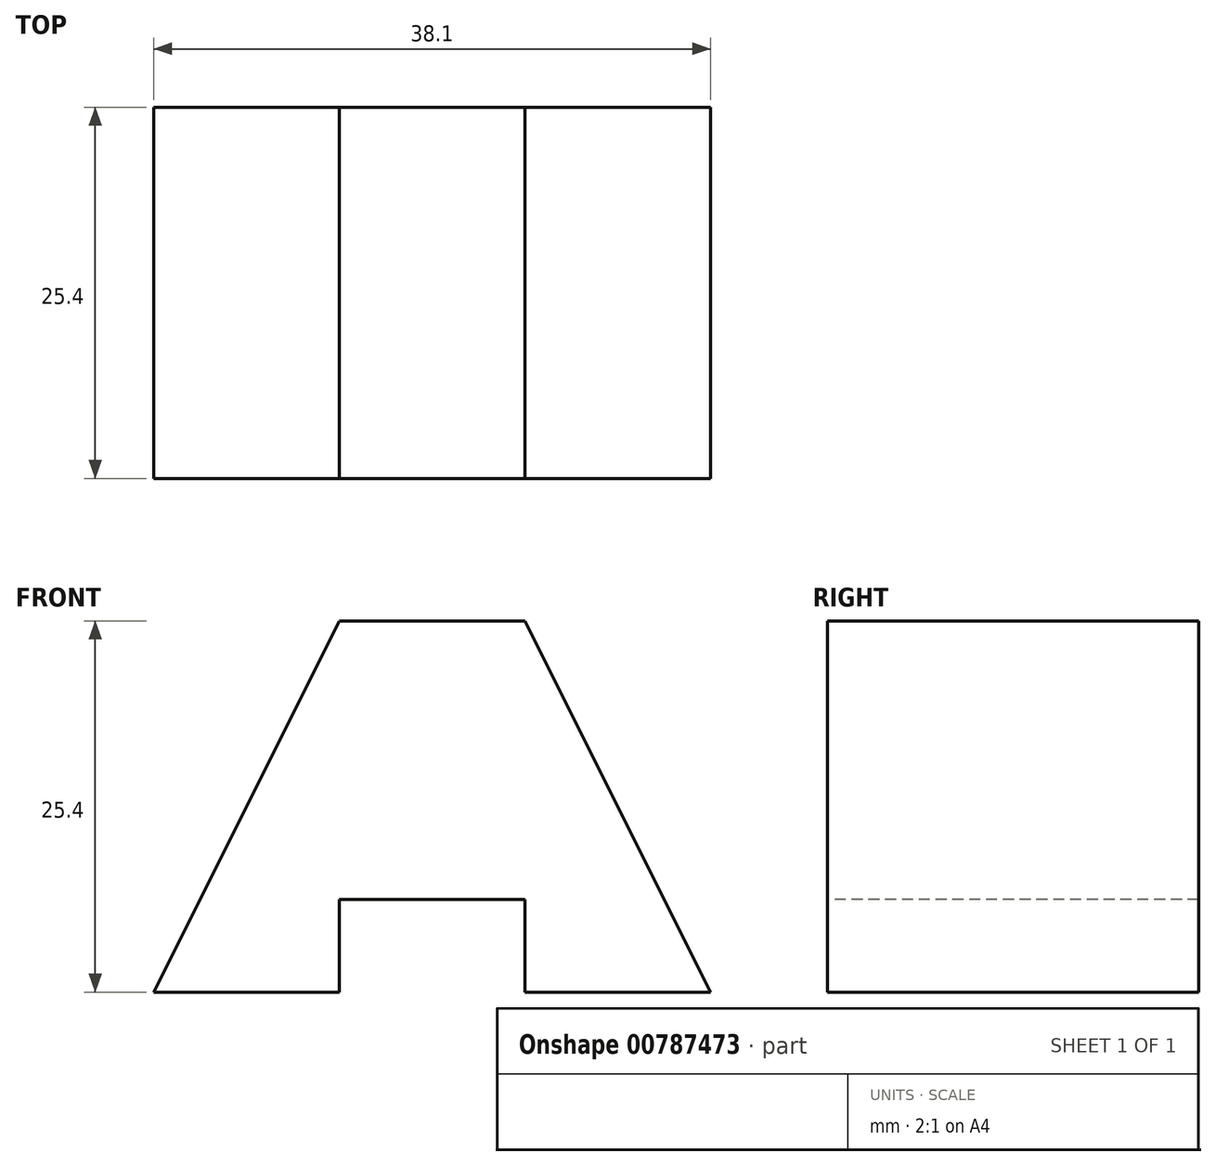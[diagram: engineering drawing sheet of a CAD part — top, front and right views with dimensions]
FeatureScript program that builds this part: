
annotation { "Feature Type Name" : "Feature", "Feature Type Description" : "" }
export const myFeature = defineFeature(function(context is Context, id is Id, definition is map)
    precondition{}
    {
        {
            var Q0;
            Q0=qCreatedBy(makeId("Front.planeOp"),FACE);
            var sketch = newSketch(context, id + "F0", { "sketchPlane" : qUnion([Q0])});
            skLineSegment(sketch, "E0", {"start": v(3, 0) * mm, "end": v(41.1, 0) * mm});
            skLineSegment(sketch, "E1", {"start": v(41.1, 0) * mm, "end": v(41.1, 25.4) * mm});
            skLineSegment(sketch, "E2", {"start": v(41.1, 25.4) * mm, "end": v(3, 25.4) * mm});
            skLineSegment(sketch, "E3", {"start": v(3, 0) * mm, "end": v(3, 25.4) * mm});
            skSolve(sketch);
        }
        {
            var Q0;
            Q0 = qSketchRegion(id + "F0", true);
            extrude(context, id + "F1", {"entities" : qUnion([Q0]), "depth" : 25.4 * mm, "offsetDistance" : 25.4 * mm});
        }
        {
            var Q0;
            Q0=makeQuery(id+"F1.opExtrude","CAP_FACE",FACE,{"disambiguationData":[OSD([sQuery(id+"F0.wireOp",EDGE,"E0"),sQuery(id+"F0.wireOp",EDGE,"E1"),sQuery(id+"F0.wireOp",EDGE,"E2"),sQuery(id+"F0.wireOp",EDGE,"E3")])],"isStart":false});
            var sketch = newSketch(context, id + "F2", { "sketchPlane" : qUnion([Q0])});
            skLineSegment(sketch, "E4", {"start": v(3, 0) * mm, "end": v(15.7, 0) * mm});
            skLineSegment(sketch, "E5", {"start": v(15.7, 0) * mm, "end": v(15.7, 6.35) * mm});
            skLineSegment(sketch, "E6", {"start": v(15.7, 6.35) * mm, "end": v(28.4, 6.35) * mm});
            skLineSegment(sketch, "E7", {"start": v(28.4, 6.35) * mm, "end": v(28.4, 0) * mm});
            skSolve(sketch);
        }
        {
            var Q0;
            Q0 = qSketchRegion(id + "F2", true);
            var Q1;
            {var subQ0=sQuery(id+"F2.wireOp",EDGE,"E5");Q1=makeQuery(id+"F2.imprint","IMPRINT",FACE,{"disambiguationData":[TD([[makeQuery(id+"F2.imprint","IMPRINT",EDGE,{"derivedFrom":subQ0}),-1.0]])]});}
            extrude(context, id + "F3", {"entities" : qUnion([Q0, Q1]), "operationType" : NewBodyOperationType.REMOVE, "oppositeDirection" : true, "depth" : 25.4 * mm, "offsetDistance" : 25.4 * mm});
        }
        {
            var Q0;
            Q0=makeQuery(id+"F1.opExtrude","CAP_FACE",FACE,{"disambiguationData":[OSD([sQuery(id+"F0.wireOp",EDGE,"E0"),sQuery(id+"F0.wireOp",EDGE,"E1"),sQuery(id+"F0.wireOp",EDGE,"E2"),sQuery(id+"F0.wireOp",EDGE,"E3")])],"isStart":false});
            var sketch = newSketch(context, id + "F4", { "sketchPlane" : qUnion([Q0])});
            skLineSegment(sketch, "E8", {"start": v(3, 25.4) * mm, "end": v(15.7, 25.4) * mm});
            skLineSegment(sketch, "E9", {"start": v(15.7, 25.4) * mm, "end": v(3, 0) * mm});
            skSolve(sketch);
        }
        {
            var Q0;
            Q0 = qSketchRegion(id + "F4", true);
            var Q1;
            Q1=makeQuery(id+"F4.imprint","IMPRINT",FACE,{"disambiguationData":[TD([[makeQuery(id+"F4.imprint","IMPRINT",EDGE,{"derivedFrom":sQuery(id+"F4.wireOp",EDGE,"E8")}),1.0]])]});
            extrude(context, id + "F5", {"entities" : qUnion([Q0, Q1]), "operationType" : NewBodyOperationType.REMOVE, "oppositeDirection" : true, "depth" : 25.4 * mm, "offsetDistance" : 25.4 * mm});
        }
        {
            var Q0;
            Q0=makeQuery(id+"F1.opExtrude","CAP_FACE",FACE,{"disambiguationData":[OSD([sQuery(id+"F0.wireOp",EDGE,"E0"),sQuery(id+"F0.wireOp",EDGE,"E1"),sQuery(id+"F0.wireOp",EDGE,"E2"),sQuery(id+"F0.wireOp",EDGE,"E3")])],"isStart":false});
            var sketch = newSketch(context, id + "F6", { "sketchPlane" : qUnion([Q0])});
            skLineSegment(sketch, "E10", {"start": v(41.1, 25.4) * mm, "end": v(28.4, 25.4) * mm});
            skLineSegment(sketch, "E11", {"start": v(41.1, 0) * mm, "end": v(28.4, 25.4) * mm});
            skSolve(sketch);
        }
        {
            var Q0;
            Q0 = qSketchRegion(id + "F6", true);
            var Q1;
            Q1=makeQuery(id+"F6.imprint","IMPRINT",FACE,{"disambiguationData":[TD([[makeQuery(id+"F6.imprint","IMPRINT",EDGE,{"derivedFrom":sQuery(id+"F6.wireOp",EDGE,"E10")}),1.0]])]});
            extrude(context, id + "F7", {"entities" : qUnion([Q0, Q1]), "operationType" : NewBodyOperationType.REMOVE, "oppositeDirection" : true, "depth" : 25.4 * mm, "offsetDistance" : 25.4 * mm});
        }
    });
